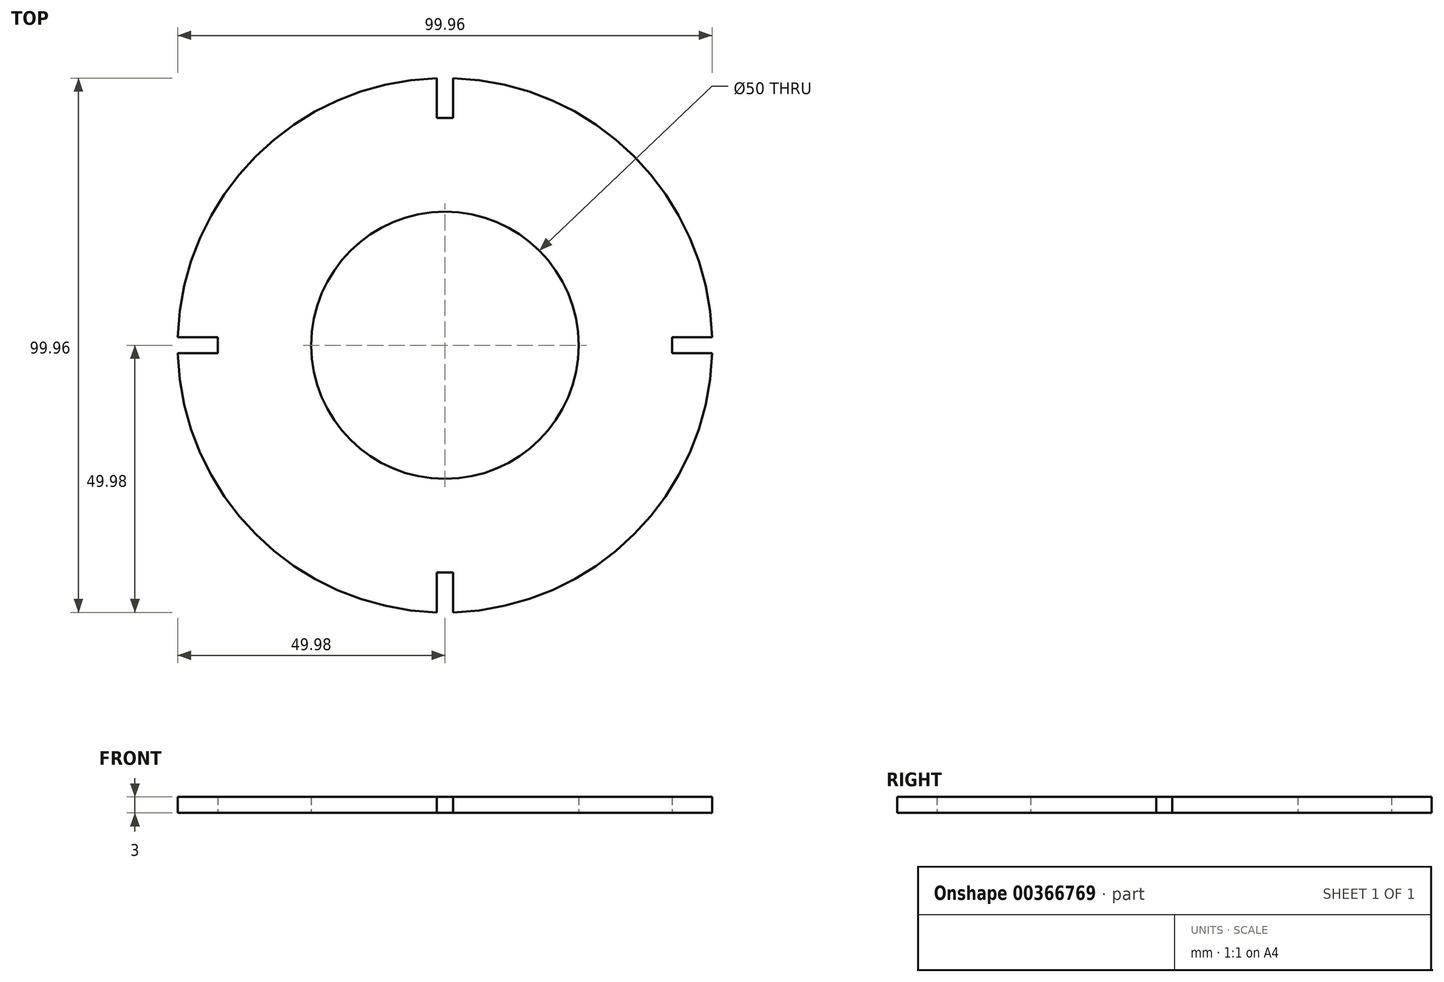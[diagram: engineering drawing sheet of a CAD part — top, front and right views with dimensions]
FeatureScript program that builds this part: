
annotation { "Feature Type Name" : "Feature", "Feature Type Description" : "" }
export const myFeature = defineFeature(function(context is Context, id is Id, definition is map)
    precondition{}
    {
        {
            var Q0;
            Q0=qCreatedBy(makeId("Top.planeOp"),FACE);
            var sketch = newSketch(context, id + "F0", { "sketchPlane" : qUnion([Q0])});
            skCircle(sketch, "E0", {"center": v(0, 0) * mm, "radius": 25 * mm});
            skArc(sketch, "E1", {"start": v(-1.5, 49.98) * mm, "mid": v(-35.36, 35.36) * mm, "end": v(-49.98, 1.5) * mm});
            skLineSegment(sketch, "E2.top", {"start": v(1.5, 42.5) * mm, "end": v(-1.5, 42.5) * mm});
            skLineSegment(sketch, "E2.left", {"start": v(1.5, 49.98) * mm, "end": v(1.5, 42.5) * mm});
            skLineSegment(sketch, "E2.right", {"start": v(-1.5, 49.98) * mm, "end": v(-1.5, 42.5) * mm});
            skPoint(sketch, "E2.middle", {"position": v(0, 50) * mm});
            skPoint(sketch, "E2.bottom.start.orphan", {"position": v(1.5, 57.5) * mm});
            skPoint(sketch, "E3.orphan", {"position": v(-1.5, 57.5) * mm});
            skLineSegment(sketch, "E4.bottom", {"start": v(49.98, -1.5) * mm, "end": v(42.5, -1.5) * mm});
            skLineSegment(sketch, "E4.top", {"start": v(49.98, 1.5) * mm, "end": v(42.5, 1.5) * mm});
            skLineSegment(sketch, "E4.right", {"start": v(42.5, -1.5) * mm, "end": v(42.5, 1.5) * mm});
            skPoint(sketch, "E4.middle", {"position": v(50, 0) * mm});
            skPoint(sketch, "E4.left.end.orphan", {"position": v(57.5, 1.5) * mm});
            skPoint(sketch, "E5.orphan", {"position": v(57.5, -1.5) * mm});
            skArc(sketch, "E6.trimOffspring", {"start": v(49.98, 1.5) * mm, "mid": v(35.36, 35.36) * mm, "end": v(1.5, 49.98) * mm});
            skLineSegment(sketch, "E7.bottom", {"start": v(-42.5, 1.5) * mm, "end": v(-49.98, 1.5) * mm});
            skLineSegment(sketch, "E7.top", {"start": v(-42.5, -1.5) * mm, "end": v(-49.98, -1.5) * mm});
            skLineSegment(sketch, "E7.left", {"start": v(-42.5, 1.5) * mm, "end": v(-42.5, -1.5) * mm});
            skPoint(sketch, "E7.middle", {"position": v(-50, 0) * mm});
            skPoint(sketch, "E7.right.start.orphan", {"position": v(-57.5, 1.5) * mm});
            skPoint(sketch, "E8.orphan", {"position": v(-57.5, -1.5) * mm});
            skArc(sketch, "E9.trimOffspring", {"start": v(-49.98, -1.5) * mm, "mid": v(-35.36, -35.36) * mm, "end": v(-1.5, -49.98) * mm});
            skLineSegment(sketch, "E10.bottom", {"start": v(1.5, -42.5) * mm, "end": v(-1.5, -42.5) * mm});
            skLineSegment(sketch, "E10.left", {"start": v(1.5, -42.5) * mm, "end": v(1.5, -49.98) * mm});
            skLineSegment(sketch, "E10.right", {"start": v(-1.5, -42.5) * mm, "end": v(-1.5, -49.98) * mm});
            skPoint(sketch, "E10.middle", {"position": v(0, -50) * mm});
            skPoint(sketch, "E10.top.end.orphan", {"position": v(-1.5, -57.5) * mm});
            skPoint(sketch, "E10.top.start.orphan", {"position": v(1.5, -57.5) * mm});
            skArc(sketch, "E11.trimOffspring", {"start": v(1.5, -49.98) * mm, "mid": v(35.36, -35.36) * mm, "end": v(49.98, -1.5) * mm});
            skSolve(sketch);
        }
        {
            var Q0;
            Q0 = qSketchRegion(id + "F0", true);
            extrude(context, id + "F1", {"entities" : qUnion([Q0]), "depth" : 3 * mm});
        }
    });
